# Revit family: VENTS-VKPFI
name_source: partatom
category: Mechanical Equipment
units: mm (PartAtom-declared; Revit-internal decimal feet)

## family parameters
Always vertical = Yes
Classification = None
Cut with Voids When Loaded = No
OmniClass Number = 23.75.35.17.11
OmniClass Title = Fans for Air Ductwork
Part Type = Breaks Into
Room Calculation Point = No
Round Connector Dimension = Use Diameter
Shared = No
Work Plane-Based = No

## types (16) — shared parameters
Casing Material = Fan Zinc
Description = Inline sound- and heat-insulated centrifugal fan for rectangular ducts
Family Version = 1.0
Load Classification = HVAC
Maintenance Zone Height = 600 mm
Maintenance Zone Material = Maintenance Zone
Manufacturer = Vents
Plastic Material = Polypropylene Black
Power Factor = 1
Protection rating = IP X4
URL = https://ventilation-system.com
dFl = 20 mm  [stored 0.0656168 ft]
handleB = 70 mm  [stored 0.229659 ft]

## per-type parameters (varying)
- VKPFI 4Е 400х200: Apparent Power=295 VA; B=400 mm  [stored 1.31234 ft]; B3=470 mm  [stored 1.54199 ft]; Connection H=200 mm  [stored 0.656168 ft]; Connection W=400 mm  [stored 1.31234 ft]; Current=1 A; DistributionBox=No; Flange=Yes; H=200 mm  [stored 0.656168 ft]; H3c=318 mm  [stored 1.04331 ft]; Handle1=Yes; Handle2=No; Hb=183 mm; Ht=135 mm; L=500 mm  [stored 1.64042 ft]; Maintenance Zone Length=500 mm  [stored 1.64042 ft]; Maintenance Zone Width=770 mm; Maximum Air Flow=1440 m³/h; Noise Level at 3 m (dBa)=42; Number of Poles=1; Power=295 W; RPM (min-1)=1350; Transported Air Temperature (°C)=-25...+40; Type Comments=Inline centrifugal fan VKPFI 4Е 400х200; Voltage=230 V; Weight=29.00 kg; dLFl=8 mm  [stored 0.0262467 ft]; eH=70 mm  [stored 0.229659 ft]; eL=120 mm  [stored 0.393701 ft]; gsD=200 mm  [stored 0.656168 ft]; handleL=145 mm  [stored 0.475722 ft]
- VKPFI 4D 400х200: Apparent Power=282 VA; B=400 mm  [stored 1.31234 ft]; B3=470 mm  [stored 1.54199 ft]; Connection H=200 mm  [stored 0.656168 ft]; Connection W=400 mm  [stored 1.31234 ft]; Current=1 A; DistributionBox=No; Flange=Yes; H=200 mm  [stored 0.656168 ft]; H3c=318 mm  [stored 1.04331 ft]; Handle1=Yes; Handle2=No; Hb=183 mm; Ht=135 mm; L=500 mm  [stored 1.64042 ft]; Maintenance Zone Length=500 mm  [stored 1.64042 ft]; Maintenance Zone Width=770 mm; Maximum Air Flow=1470 m³/h; Noise Level at 3 m (dBa)=43; Number of Poles=3; Power=282 W; RPM (min-1)=1300; Transported Air Temperature (°C)=-25...+45; Type Comments=Inline centrifugal fan VKPFI 4D 400х200; Voltage=400 V; Weight=29.00 kg; dLFl=8 mm  [stored 0.0262467 ft]; eH=70 mm  [stored 0.229659 ft]; eL=120 mm  [stored 0.393701 ft]; gsD=200 mm  [stored 0.656168 ft]; handleL=145 mm  [stored 0.475722 ft]
- VKPFI 4Е 500х250: Apparent Power=535 VA; B=500 mm  [stored 1.64042 ft]; B3=570 mm  [stored 1.87008 ft]; Connection H=250 mm  [stored 0.82021 ft]; Connection W=500 mm  [stored 1.64042 ft]; Current=2 A; DistributionBox=No; Flange=Yes; H=250 mm  [stored 0.82021 ft]; H3c=366 mm; Handle1=Yes; Handle2=No; Hb=208 mm  [stored 0.682415 ft]; Ht=158 mm; L=640 mm  [stored 2.09974 ft]; Maintenance Zone Length=640 mm  [stored 2.09974 ft]; Maintenance Zone Width=870 mm; Maximum Air Flow=1750 m³/h; Noise Level at 3 m (dBa)=44; Number of Poles=1; Power=535 W; RPM (min-1)=1250; Transported Air Temperature (°C)=-20...+40; Type Comments=Inline centrifugal fan VKPFI 4Е 500х250; Voltage=230 V; Weight=40.50 kg; dLFl=8 mm  [stored 0.0262467 ft]; eH=70 mm  [stored 0.229659 ft]; eL=150 mm  [stored 0.492126 ft]; gsD=250 mm  [stored 0.82021 ft]; handleL=145 mm  [stored 0.475722 ft]
- VKPFI 4D 500х250: Apparent Power=570 VA; B=500 mm  [stored 1.64042 ft]; B3=570 mm  [stored 1.87008 ft]; Connection H=250 mm  [stored 0.82021 ft]; Connection W=500 mm  [stored 1.64042 ft]; Current=1 A; DistributionBox=No; Flange=Yes; H=250 mm  [stored 0.82021 ft]; H3c=366 mm; Handle1=Yes; Handle2=No; Hb=208 mm  [stored 0.682415 ft]; Ht=158 mm; L=640 mm  [stored 2.09974 ft]; Maintenance Zone Length=640 mm  [stored 2.09974 ft]; Maintenance Zone Width=870 mm; Maximum Air Flow=1850 m³/h; Noise Level at 3 m (dBa)=44; Number of Poles=3; Power=570 W; RPM (min-1)=1270; Transported Air Temperature (°C)=-20...+40; Type Comments=Inline centrifugal fan VKPFI 4D 500х250; Voltage=400 V; Weight=40.50 kg; dLFl=8 mm  [stored 0.0262467 ft]; eH=70 mm  [stored 0.229659 ft]; eL=150 mm  [stored 0.492126 ft]; gsD=250 mm  [stored 0.82021 ft]; handleL=145 mm  [stored 0.475722 ft]
- VKPFI 4Е 500х300: Apparent Power=710 VA; B=500 mm  [stored 1.64042 ft]; B3=570 mm  [stored 1.87008 ft]; Connection H=300 mm  [stored 0.984252 ft]; Connection W=500 mm  [stored 1.64042 ft]; Current=3 A; DistributionBox=No; Flange=Yes; H=300 mm  [stored 0.984252 ft]; H3c=416 mm; Handle1=Yes; Handle2=No; Hb=234 mm  [stored 0.767717 ft]; Ht=182 mm  [stored 0.597113 ft]; L=680 mm; Maintenance Zone Length=680 mm; Maintenance Zone Width=870 mm; Maximum Air Flow=2350 m³/h; Noise Level at 3 m (dBa)=47; Number of Poles=1; Power=710 W; RPM (min-1)=1230; Transported Air Temperature (°C)=-25...+70; Type Comments=Inline centrifugal fan VKPFI 4Е 500х300; Voltage=230 V; Weight=52.50 kg; dLFl=8 mm  [stored 0.0262467 ft]; eH=70 mm  [stored 0.229659 ft]; eL=170 mm  [stored 0.557743 ft]; gsD=250 mm  [stored 0.82021 ft]; handleL=145 mm  [stored 0.475722 ft]
- VKPFI 4D 500х300: Apparent Power=855 VA; B=500 mm  [stored 1.64042 ft]; B3=570 mm  [stored 1.87008 ft]; Connection H=300 mm  [stored 0.984252 ft]; Connection W=500 mm  [stored 1.64042 ft]; Current=2 A; DistributionBox=No; Flange=Yes; H=300 mm  [stored 0.984252 ft]; H3c=416 mm; Handle1=Yes; Handle2=No; Hb=234 mm  [stored 0.767717 ft]; Ht=182 mm  [stored 0.597113 ft]; L=680 mm; Maintenance Zone Length=680 mm; Maintenance Zone Width=870 mm; Maximum Air Flow=2350 m³/h; Noise Level at 3 m (dBa)=47; Number of Poles=3; Power=855 W; RPM (min-1)=1300; Transported Air Temperature (°C)=-25...+50; Type Comments=Inline centrifugal fan VKPFI 4D 500х300; Voltage=400 V; Weight=52.50 kg; dLFl=8 mm  [stored 0.0262467 ft]; eH=70 mm  [stored 0.229659 ft]; eL=170 mm  [stored 0.557743 ft]; gsD=250 mm  [stored 0.82021 ft]; handleL=145 mm  [stored 0.475722 ft]
- VKPFI 4Е 600х300: Apparent Power=1240 VA; B=600 mm; B3=670 mm; Connection H=300 mm  [stored 0.984252 ft]; Connection W=600 mm; Current=6 A; DistributionBox=No; Flange=Yes; H=300 mm  [stored 0.984252 ft]; H3c=436 mm  [stored 1.43045 ft]; Handle1=Yes; Handle2=No; Hb=254 mm; Ht=182 mm  [stored 0.597113 ft]; L=680 mm; Maintenance Zone Length=680 mm; Maintenance Zone Width=970 mm; Maximum Air Flow=2950 m³/h; Noise Level at 3 m (dBa)=51; Number of Poles=1; Power=1240 W; RPM (min-1)=1210; Transported Air Temperature (°C)=-25...+50; Type Comments=Inline centrifugal fan VKPFI 4Е 600х300; Voltage=230 V; Weight=56.00 kg; dLFl=8 mm  [stored 0.0262467 ft]; eH=70 mm  [stored 0.229659 ft]; eL=120 mm  [stored 0.393701 ft]; gsD=300 mm  [stored 0.984252 ft]; handleL=145 mm  [stored 0.475722 ft]
- VKPFI 4D 600х300: Apparent Power=1560 VA; B=600 mm; B3=670 mm; Connection H=300 mm  [stored 0.984252 ft]; Connection W=600 mm; Current=3 A; DistributionBox=No; Flange=Yes; H=300 mm  [stored 0.984252 ft]; H3c=436 mm  [stored 1.43045 ft]; Handle1=Yes; Handle2=No; Hb=254 mm; Ht=182 mm  [stored 0.597113 ft]; L=680 mm; Maintenance Zone Length=680 mm; Maintenance Zone Width=970 mm; Maximum Air Flow=3740 m³/h; Noise Level at 3 m (dBa)=50; Number of Poles=3; Power=1560 W; RPM (min-1)=1310; Transported Air Temperature (°C)=-25...+65; Type Comments=Inline centrifugal fan VKPFI 4D 600х300; Voltage=400 V; Weight=56.00 kg; dLFl=8 mm  [stored 0.0262467 ft]; eH=70 mm  [stored 0.229659 ft]; eL=120 mm  [stored 0.393701 ft]; gsD=300 mm  [stored 0.984252 ft]; handleL=145 mm  [stored 0.475722 ft]
- VKPFI 4Е 600х350: Apparent Power=2480 VA; B=600 mm; B3=670 mm; Connection H=350 mm  [stored 1.14829 ft]; Connection W=600 mm; Current=14 A; DistributionBox=No; Flange=Yes; H=350 mm  [stored 1.14829 ft]; H3c=488 mm  [stored 1.60105 ft]; Handle1=Yes; Handle2=No; Hb=280 mm  [stored 0.918635 ft]; Ht=208 mm  [stored 0.682415 ft]; L=735 mm; Maintenance Zone Length=735 mm; Maintenance Zone Width=970 mm; Maximum Air Flow=4260 m³/h; Noise Level at 3 m (dBa)=51; Number of Poles=1; Power=2480 W; RPM (min-1)=1260; Transported Air Temperature (°C)=-20...+40; Type Comments=Inline centrifugal fan VKPFI 4Е 600х350; Voltage=230 V; Weight=72.00 kg; dLFl=8 mm  [stored 0.0262467 ft]; eH=70 mm  [stored 0.229659 ft]; eL=180 mm  [stored 0.590551 ft]; gsD=300 mm  [stored 0.984252 ft]; handleL=145 mm  [stored 0.475722 ft]
- VKPFI 4D 600х350: Apparent Power=2460 VA; B=600 mm; B3=670 mm; Connection H=350 mm  [stored 1.14829 ft]; Connection W=600 mm; Current=4 A; DistributionBox=No; Flange=Yes; H=350 mm  [stored 1.14829 ft]; H3c=488 mm  [stored 1.60105 ft]; Handle1=Yes; Handle2=No; Hb=280 mm  [stored 0.918635 ft]; Ht=208 mm  [stored 0.682415 ft]; L=735 mm; Maintenance Zone Length=735 mm; Maintenance Zone Width=970 mm; Maximum Air Flow=5020 m³/h; Noise Level at 3 m (dBa)=52; Number of Poles=3; Power=2460 W; RPM (min-1)=1300; Transported Air Temperature (°C)=-20...+40; Type Comments=Inline centrifugal fan VKPFI 4D 600х350; Voltage=400 V; Weight=72.00 kg; dLFl=8 mm  [stored 0.0262467 ft]; eH=70 mm  [stored 0.229659 ft]; eL=180 mm  [stored 0.590551 ft]; gsD=300 mm  [stored 0.984252 ft]; handleL=145 mm  [stored 0.475722 ft]
- VKPFI 4D 700х400: Apparent Power=3630 VA; B=700 mm; B3=800 mm; Connection H=400 mm  [stored 1.31234 ft]; Connection W=700 mm; Current=6 A; DistributionBox=Yes; Flange=No; H=400 mm  [stored 1.31234 ft]; H3c=574 mm  [stored 1.8832 ft]; Handle1=No; Handle2=Yes; Hb=322 mm  [stored 1.05643 ft]; Ht=252 mm; L=880 mm; Maintenance Zone Length=880 mm; Maintenance Zone Width=1100 mm; Maximum Air Flow=6450 m³/h; Noise Level at 3 m (dBa)=56; Number of Poles=3; Power=3630 W; RPM (min-1)=1320; Transported Air Temperature (°C)=-25...+40; Type Comments=Inline centrifugal fan VKPFI 4D 700х400; Voltage=400 V; Weight=103.00 kg; dLFl=0 mm  [stored 0 ft]; eH=212 mm  [stored 0.695538 ft]; eL=372 mm  [stored 1.22047 ft]; gsD=350 mm  [stored 1.14829 ft]; handleL=145 mm  [stored 0.475722 ft]
- VKPFI 6D 700х400: Apparent Power=1150 VA; B=700 mm; B3=800 mm; Connection H=400 mm  [stored 1.31234 ft]; Connection W=700 mm; Current=2 A; DistributionBox=Yes; Flange=No; H=400 mm  [stored 1.31234 ft]; H3c=574 mm  [stored 1.8832 ft]; Handle1=No; Handle2=Yes; Hb=322 mm  [stored 1.05643 ft]; Ht=252 mm; L=880 mm; Maintenance Zone Length=880 mm; Maintenance Zone Width=1100 mm; Maximum Air Flow=4050 m³/h; Noise Level at 3 m (dBa)=49; Number of Poles=3; Power=1150 W; RPM (min-1)=890; Transported Air Temperature (°C)=-20...+70; Type Comments=Inline centrifugal fan VKPFI 6D 700х400; Voltage=400 V; Weight=99.00 kg; dLFl=0 mm  [stored 0 ft]; eH=212 mm  [stored 0.695538 ft]; eL=372 mm  [stored 1.22047 ft]; gsD=350 mm  [stored 1.14829 ft]; handleL=145 mm  [stored 0.475722 ft]
- VKPFI 4D 800х500: Apparent Power=5850 VA; B=800 mm; B3=900 mm; Connection H=500 mm  [stored 1.64042 ft]; Connection W=800 mm; Current=9 A; DistributionBox=Yes; Flange=No; H=500 mm  [stored 1.64042 ft]; H3c=674 mm; Handle1=No; Handle2=Yes; Hb=372 mm  [stored 1.22047 ft]; Ht=302 mm; L=935 mm; Maintenance Zone Length=935 mm; Maintenance Zone Width=1200 mm; Maximum Air Flow=8120 m³/h; Noise Level at 3 m (dBa)=61; Number of Poles=3; Power=5850 W; RPM (min-1)=1140; Transported Air Temperature (°C)=-25...+40; Type Comments=Inline centrifugal fan VKPFI 4D 800х500; Voltage=400 V; Weight=120.00 kg; dLFl=0 mm  [stored 0 ft]; eH=212 mm  [stored 0.695538 ft]; eL=372 mm  [stored 1.22047 ft]; gsD=400 mm  [stored 1.31234 ft]; handleL=145 mm  [stored 0.475722 ft]
- VKPFI 6D 800х500: Apparent Power=2790 VA; B=800 mm; B3=900 mm; Connection H=500 mm  [stored 1.64042 ft]; Connection W=800 mm; Current=5 A; DistributionBox=Yes; Flange=No; H=500 mm  [stored 1.64042 ft]; H3c=674 mm; Handle1=No; Handle2=Yes; Hb=372 mm  [stored 1.22047 ft]; Ht=302 mm; L=935 mm; Maintenance Zone Length=935 mm; Maintenance Zone Width=1200 mm; Maximum Air Flow=7610 m³/h; Noise Level at 3 m (dBa)=53; Number of Poles=3; Power=2790 W; RPM (min-1)=830; Transported Air Temperature (°C)=-20...+50; Type Comments=Inline centrifugal fan VKPFI 6D 800х500; Voltage=400 V; Weight=127.00 kg; dLFl=0 mm  [stored 0 ft]; eH=212 mm  [stored 0.695538 ft]; eL=372 mm  [stored 1.22047 ft]; gsD=400 mm  [stored 1.31234 ft]; handleL=145 mm  [stored 0.475722 ft]
- VKPFI 6D 900х500: Apparent Power=3870 VA; B=900 mm; B3=1000 mm; Connection H=500 mm  [stored 1.64042 ft]; Connection W=900 mm; Current=7 A; DistributionBox=Yes; Flange=No; H=500 mm  [stored 1.64042 ft]; H3c=674 mm; Handle1=No; Handle2=Yes; Hb=372 mm  [stored 1.22047 ft]; Ht=302 mm; L=1000 mm; Maintenance Zone Length=1000 mm; Maintenance Zone Width=1300 mm; Maximum Air Flow=9540 m³/h; Noise Level at 3 m (dBa)=55; Number of Poles=3; Power=3870 W; RPM (min-1)=930; Transported Air Temperature (°C)=-20...+55; Type Comments=Inline centrifugal fan VKPFI 6D 900х500; Voltage=400 V; Weight=142.00 kg; dLFl=0 mm  [stored 0 ft]; eH=212 mm  [stored 0.695538 ft]; eL=372 mm  [stored 1.22047 ft]; gsD=450 mm  [stored 1.47638 ft]; handleL=175 mm  [stored 0.574147 ft]
- VKPFI 6D 1000х500: Apparent Power=3870 VA; B=1000 mm; B3=1100 mm; Connection H=500 mm  [stored 1.64042 ft]; Connection W=1000 mm; Current=7 A; DistributionBox=Yes; Flange=No; H=500 mm  [stored 1.64042 ft]; H3c=674 mm; Handle1=No; Handle2=Yes; Hb=372 mm  [stored 1.22047 ft]; Ht=302 mm; L=1000 mm; Maintenance Zone Length=1000 mm; Maintenance Zone Width=1400 mm; Maximum Air Flow=9540 m³/h; Noise Level at 3 m (dBa)=55; Number of Poles=3; Power=3870 W; RPM (min-1)=930; Transported Air Temperature (°C)=-20...+55; Type Comments=Inline centrifugal fan VKPFI 6D 1000х500; Voltage=400 V; Weight=150.00 kg; dLFl=0 mm  [stored 0 ft]; eH=212 mm  [stored 0.695538 ft]; eL=372 mm  [stored 1.22047 ft]; gsD=500 mm  [stored 1.64042 ft]; handleL=175 mm  [stored 0.574147 ft]

note: column(s) folded — value = type name in every type: Model

note: [stored X ft] marks values corroborated as IEEE doubles in the binary element streams (Revit-internal decimal feet)

## geometry (parser evidence)
native form markers: Sweep x11
no freeform markers — native parametric forms only
